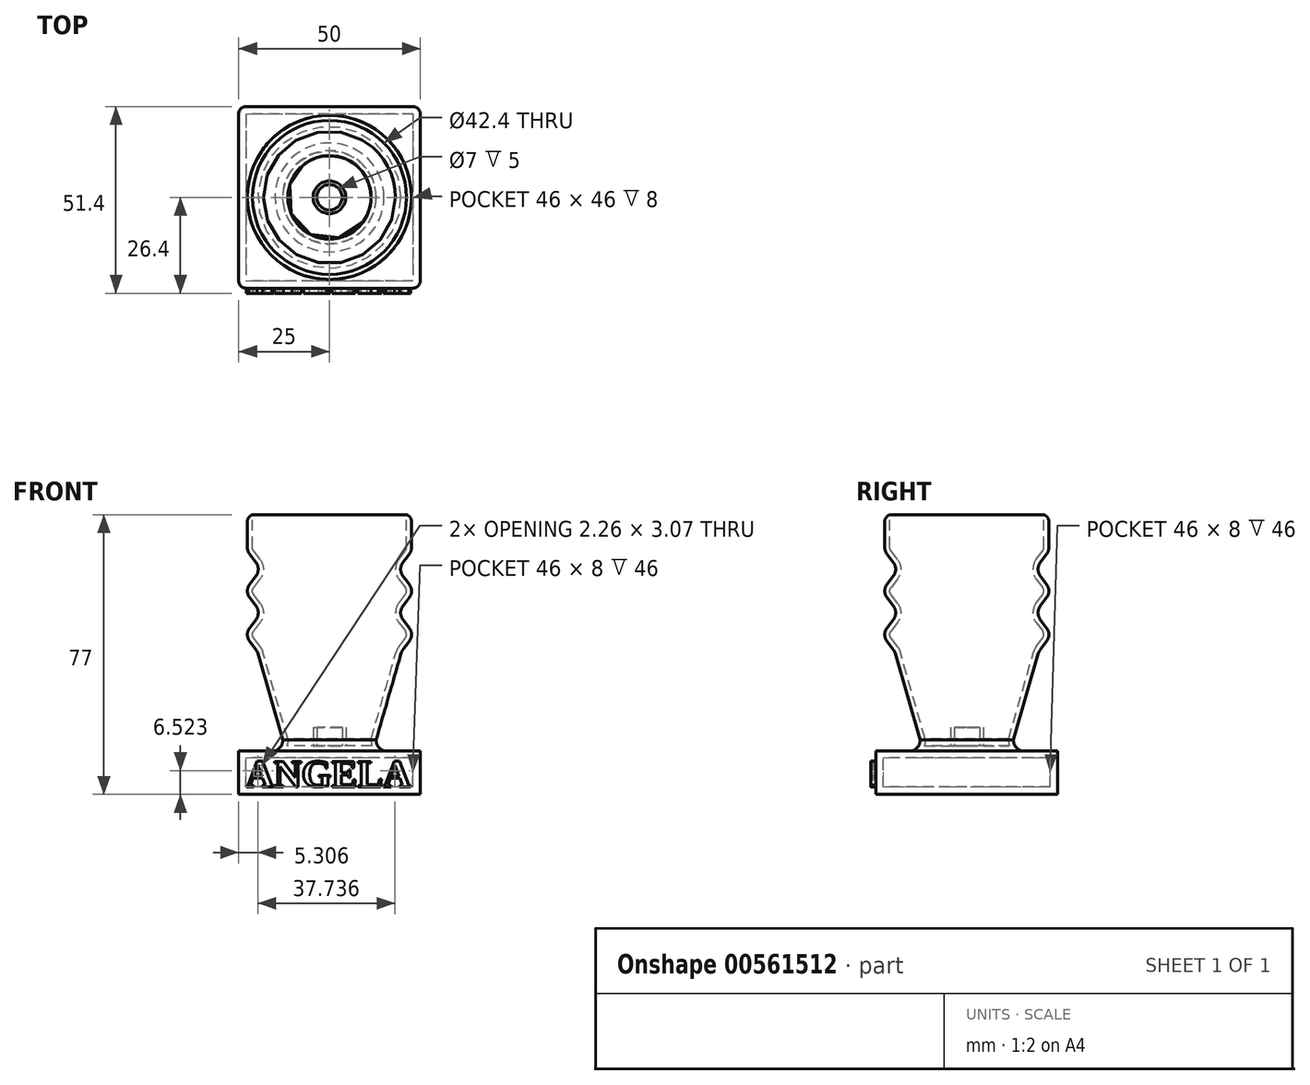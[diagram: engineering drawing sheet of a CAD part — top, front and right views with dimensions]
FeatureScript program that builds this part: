
annotation { "Feature Type Name" : "Feature", "Feature Type Description" : "" }
export const myFeature = defineFeature(function(context is Context, id is Id, definition is map)
    precondition{}
    {
        {
            var Q0;
            Q0=qCreatedBy(makeId("Top.planeOp"),FACE);
            var sketch = newSketch(context, id + "F0", { "sketchPlane" : qUnion([Q0])});
            skLineSegment(sketch, "E0.bottom", {"start": v(25, 25) * mm, "end": v(-25, 25) * mm});
            skLineSegment(sketch, "E0.top", {"start": v(25, -25) * mm, "end": v(-25, -25) * mm});
            skLineSegment(sketch, "E0.left", {"start": v(25, 25) * mm, "end": v(25, -25) * mm});
            skLineSegment(sketch, "E0.right", {"start": v(-25, 25) * mm, "end": v(-25, -25) * mm});
            skPoint(sketch, "E0.middle", {"position": v(0, 0) * mm});
            skSolve(sketch);
        }
        {
            var Q0;
            Q0 = qSketchRegion(id + "F0", true);
            extrude(context, id + "F1", {"entities" : qUnion([Q0]), "depth" : 12 * mm, "offsetDistance" : 25 * mm});
        }
        {
            var Q0;
            Q0=makeQuery(id+"F1.opExtrude","SWEPT_FACE",FACE,{"disambiguationData":[OSD([sQuery(id+"F0.wireOp",EDGE,"E0.top")])]});
            var sketch = newSketch(context, id + "F2", { "sketchPlane" : qUnion([Q0])});
            skText(sketch, "E1", { "text": "ANGELA", "fontName": "Tinos-Bold.ttf"});
            const initialGuessF2  = {"E1": [-0.023, 0.0021, 1, 0, 0.00764]};
            skSetInitialGuess(sketch, initialGuessF2);
            skSolve(sketch);
        }
        {
            var Q0;
            Q0 = qSketchRegion(id + "F2", true);
            extrude(context, id + "F3", {"entities" : qUnion([Q0]), "depth" : 1.4 * mm, "offsetDistance" : 25 * mm});
        }
        {
            var Q0;
            Q0=makeQuery(id+"F1.opExtrude","SWEPT_EDGE",EDGE,{"disambiguationData":[OSD([sQuery(id+"F0.wireOp",EDGE,"E0.top"),sQuery(id+"F0.wireOp",EDGE,"E0.right")])]});
            var Q1;
            Q1=makeQuery(id+"F1.opExtrude","SWEPT_EDGE",EDGE,{"disambiguationData":[OSD([sQuery(id+"F0.wireOp",EDGE,"E0.bottom"),sQuery(id+"F0.wireOp",EDGE,"E0.right")])]});
            var Q2;
            Q2=makeQuery(id+"F1.opExtrude","SWEPT_EDGE",EDGE,{"disambiguationData":[OSD([sQuery(id+"F0.wireOp",EDGE,"E0.top"),sQuery(id+"F0.wireOp",EDGE,"E0.left")])]});
            var Q3;
            Q3=makeQuery(id+"F1.opExtrude","SWEPT_EDGE",EDGE,{"disambiguationData":[OSD([sQuery(id+"F0.wireOp",EDGE,"E0.bottom"),sQuery(id+"F0.wireOp",EDGE,"E0.left")])]});
            fillet(context, id + "F4", {"entities" : qUnion([Q0, Q1, Q2, Q3]), "radius" : 2 * mm, "tangentPropagation" : true, "allowEdgeOverflow" : false});
        }
        {
            var Q0;
            Q0=qCreatedBy(makeId("Front.planeOp"),FACE);
            var sketch = newSketch(context, id + "F5", { "sketchPlane" : qUnion([Q0])});
            skLineSegment(sketch, "E2", {"start": v(0, 0) * mm, "end": v(0, 77) * mm, "construction": true});
            skLineSegment(sketch, "E3", {"start": v(0, 77) * mm, "end": v(-22.6, 77) * mm});
            skLineSegment(sketch, "E4", {"start": v(0, 12) * mm, "end": v(-12, 12) * mm});
            skLineSegment(sketch, "E5", {"start": v(-22.6, 77) * mm, "end": v(-22.6, 68) * mm, "construction": true});
            skArc(sketch, "E6", {"start": v(-20.2, 60.2) * mm, "mid": v(-19.6, 62) * mm, "end": v(-20.2, 63.8) * mm});
            skLineSegment(sketch, "E7", {"start": v(-19.6, 77) * mm, "end": v(-19.6, 35) * mm, "construction": true});
            skArc(sketch, "E8", {"start": v(-22, 57.8) * mm, "mid": v(-22.6, 56) * mm, "end": v(-22, 54.2) * mm});
            skLineSegment(sketch, "E9", {"start": v(-22, 57.8) * mm, "end": v(-20.2, 60.2) * mm});
            skLineSegment(sketch, "E10", {"start": v(-22.6, 77) * mm, "end": v(-22.6, 68) * mm});
            skArc(sketch, "E11", {"start": v(-20.2, 48.2) * mm, "mid": v(-19.6, 50) * mm, "end": v(-20.2, 51.8) * mm});
            skLineSegment(sketch, "E12", {"start": v(-22, 54.2) * mm, "end": v(-20.2, 51.8) * mm});
            skArc(sketch, "E13", {"start": v(-22, 45.8) * mm, "mid": v(-22.6, 44) * mm, "end": v(-22, 42.2) * mm});
            skLineSegment(sketch, "E14", {"start": v(-20.2, 48.2) * mm, "end": v(-22, 45.8) * mm});
            skArc(sketch, "E15", {"start": v(-19.6, 38) * mm, "mid": v(-19.75, 38.95) * mm, "end": v(-20.2, 39.8) * mm});
            skLineSegment(sketch, "E16", {"start": v(-22, 42.2) * mm, "end": v(-20.2, 39.8) * mm});
            skArc(sketch, "E17", {"start": v(-22.6, 68) * mm, "mid": v(-22.45, 67.05) * mm, "end": v(-22, 66.2) * mm});
            skLineSegment(sketch, "E18", {"start": v(-22, 66.2) * mm, "end": v(-20.2, 63.8) * mm});
            skLineSegment(sketch, "E19.trimOffspring", {"start": v(-22.6, 65) * mm, "end": v(-22.6, 47) * mm, "construction": true});
            skLineSegment(sketch, "E20", {"start": v(-19.72, 38.83) * mm, "end": v(-12.86, 15) * mm});
            skLineSegment(sketch, "E21", {"start": v(0, 77) * mm, "end": v(0, 12) * mm});
            skArc(sketch, "E22", {"start": v(-15, 12) * mm, "mid": v(-13.42, 13.13) * mm, "end": v(-12.86, 15) * mm});
            skLineSegment(sketch, "E23", {"start": v(-15, 12) * mm, "end": v(-12, 12) * mm});
            skSolve(sketch);
        }
        {
            var Q0;
            Q0 = qSketchRegion(id + "F5", true);
            var Q1;
            Q1=sQuery(id+"F5.wireOp",EDGE,"E21");
            revolve(context, id + "F6", {"entities" : qUnion([Q0]), "axis" : qUnion([Q1]), "revolveType" : RevolveType.FULL});
        }
        {
            var Q0;
            Q0=makeQuery(id+"F6.opRevolve","SWEPT_FACE",FACE,{"disambiguationData":[OSD([sQuery(id+"F5.wireOp",EDGE,"E3")])]});
            shell(context, id + "F7", {"entities" : qUnion([Q0]), "thickness" : 1.4 * mm});
        }
        {
            var Q0;
            Q0=makeQuery(id+"F6.opRevolve","SWEPT_EDGE",EDGE,{"disambiguationData":[OSD([sQuery(id+"F5.wireOp",EDGE,"E3"),sQuery(id+"F5.wireOp",EDGE,"E10")])]});
            fillet(context, id + "F8", {"entities" : qUnion([Q0]), "radius" : 2 * mm, "tangentPropagation" : true, "allowEdgeOverflow" : false});
        }
        {
            var Q0;
            Q0=makeQuery(id+"F7.opShell","OFFSET_FACE",FACE,{"disambiguationData":[OSD([sQuery(id+"F5.wireOp",EDGE,"E4")])]});
            var sketch = newSketch(context, id + "F9", { "sketchPlane" : qUnion([Q0])});
            skCircle(sketch, "E24", {"center": v(0, 0) * mm, "radius": 3.5 * mm});
            skCircle(sketch, "E25", {"center": v(0, 0) * mm, "radius": 4.5 * mm});
            skSolve(sketch);
        }
        {
            var Q0;
            Q0 = qSketchRegion(id + "F9", true);
            extrude(context, id + "F10", {"entities" : qUnion([Q0]), "operationType" : NewBodyOperationType.ADD, "depth" : 5 * mm, "offsetDistance" : 25 * mm});
        }
        {
            var Q0;
            Q0=makeQuery(id+"F1.opExtrude","SWEPT_FACE",FACE,{"disambiguationData":[OSD([sQuery(id+"F0.wireOp",EDGE,"E0.left")])]});
            var Q1;
            Q1=makeQuery(id+"F1.opExtrude","SWEPT_BODY",BODY,{"disambiguationData":[OSD([sQuery(id+"F0.wireOp",EDGE,"E0.bottom"),sQuery(id+"F0.wireOp",EDGE,"E0.top"),sQuery(id+"F0.wireOp",EDGE,"E0.left"),sQuery(id+"F0.wireOp",EDGE,"E0.right")])]});
            shell(context, id + "F11", {"isHollow" : true, "entities" : qUnion([Q0]), "parts" : qUnion([Q1]), "thickness" : 2 * mm});
        }
    });
